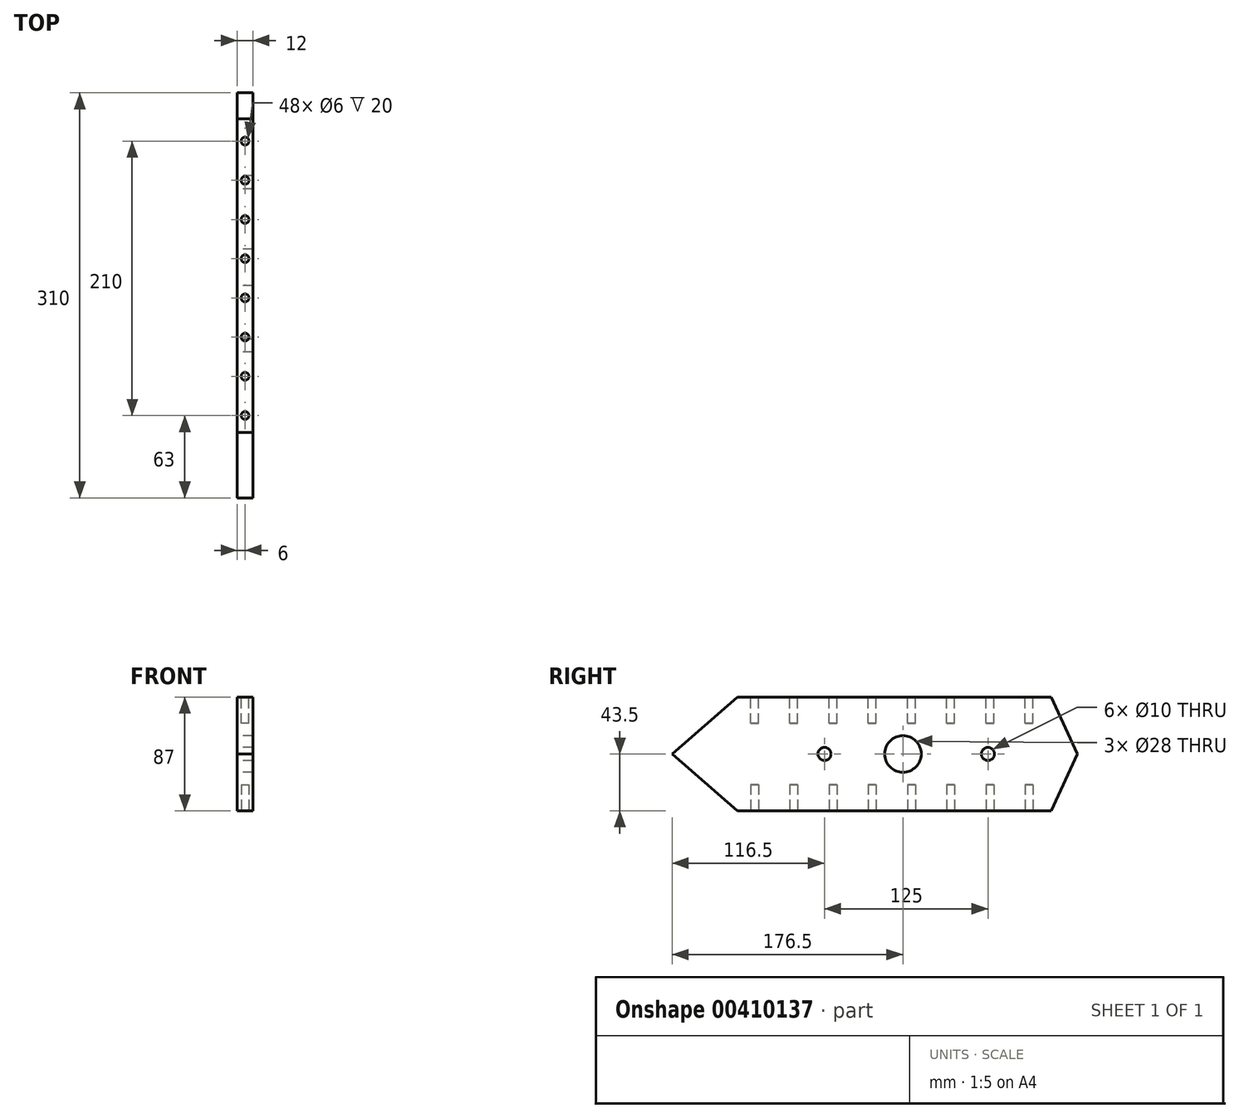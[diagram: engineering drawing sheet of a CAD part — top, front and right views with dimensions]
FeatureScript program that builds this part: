
annotation { "Feature Type Name" : "Feature", "Feature Type Description" : "" }
export const myFeature = defineFeature(function(context is Context, id is Id, definition is map)
    precondition{}
    {
        {
            var Q0;
            Q0=qCreatedBy(makeId("Right.planeOp"),FACE);
            var sketch = newSketch(context, id + "F0", { "sketchPlane" : qUnion([Q0])});
            skLineSegment(sketch, "E0.bottom", {"start": v(0, 0) * mm, "end": v(240, 0) * mm});
            skLineSegment(sketch, "E0.top", {"start": v(0, 87) * mm, "end": v(240, 87) * mm});
            skLineSegment(sketch, "E0.left", {"start": v(0, 0) * mm, "end": v(0, 87) * mm, "construction": true});
            skLineSegment(sketch, "E0.right", {"start": v(240, 0) * mm, "end": v(240, 87) * mm, "construction": true});
            skLineSegment(sketch, "E1", {"start": v(0, 43.5) * mm, "end": v(240, 43.5) * mm, "construction": true});
            skPoint(sketch, "E2", {"position": v(126.5, 43.5) * mm});
            skLineSegment(sketch, "E3", {"start": v(240, 87) * mm, "end": v(260, 43.5) * mm});
            skLineSegment(sketch, "E4", {"start": v(260, 43.5) * mm, "end": v(240, 0) * mm});
            skLineSegment(sketch, "E5", {"start": v(0, 87) * mm, "end": v(-50, 43.5) * mm});
            skLineSegment(sketch, "E6", {"start": v(-50, 43.5) * mm, "end": v(0, 0) * mm});
            skLineSegment(sketch, "E7", {"start": v(240, 43.5) * mm, "end": v(260, 43.5) * mm, "construction": true});
            skLineSegment(sketch, "E8", {"start": v(0, 43.5) * mm, "end": v(-50, 43.5) * mm, "construction": true});
            skCircle(sketch, "E9", {"center": v(126.5, 43.5) * mm, "radius": 14 * mm});
            skCircle(sketch, "E10", {"center": v(191.5, 43.5) * mm, "radius": 5 * mm});
            skCircle(sketch, "E11", {"center": v(66.5, 43.5) * mm, "radius": 5 * mm});
            skSolve(sketch);
        }
        {
            var Q0;
            Q0=qSketchRegion(id+"F0",true);
            extrude(context, id + "F1", {"entities" : qUnion([Q0]), "depth" : 12 * mm});
        }
        {
            var Q0;
            Q0=makeQuery(id+"F1.opExtrude","SWEPT_FACE",FACE,{"disambiguationData":[OSD([sQuery(id+"F0.wireOp",EDGE,"E0.top")])]});
            var sketch = newSketch(context, id + "F2", { "sketchPlane" : qUnion([Q0])});
            skLineSegment(sketch, "E12", {"start": v(6, 240) * mm, "end": v(6, 0) * mm, "construction": true});
            skCircle(sketch, "E13", {"center": v(6, 13) * mm, "radius": 3 * mm});
            skCircle(sketch, "E14.0.1.0", {"center": v(6, 43) * mm, "radius": 3 * mm});
            skCircle(sketch, "E14.0.2.0", {"center": v(6, 73) * mm, "radius": 3 * mm});
            skCircle(sketch, "E14.0.3.0", {"center": v(6, 103) * mm, "radius": 3 * mm});
            skCircle(sketch, "E14.0.4.0", {"center": v(6, 133) * mm, "radius": 3 * mm});
            skCircle(sketch, "E14.0.5.0", {"center": v(6, 163) * mm, "radius": 3 * mm});
            skCircle(sketch, "E14.0.6.0", {"center": v(6, 193) * mm, "radius": 3 * mm});
            skCircle(sketch, "E14.0.7.0", {"center": v(6, 223) * mm, "radius": 3 * mm});
            skLineSegment(sketch, "E14.direction1", {"start": v(6, 13) * mm, "end": v(31, 13) * mm, "construction": true});
            skLineSegment(sketch, "E14.direction2", {"start": v(6, 13) * mm, "end": v(6, 43) * mm, "construction": true});
            skSolve(sketch);
        }
        {
            var Q0;
            Q0 = qSketchRegion(id + "F2", true);
            extrude(context, id + "F3", {"entities" : qUnion([Q0]), "operationType" : NewBodyOperationType.REMOVE, "oppositeDirection" : true, "depth" : 20 * mm});
        }
        {
            var Q0;
            Q0=makeQuery(id+"F1.opExtrude","SWEPT_FACE",FACE,{"disambiguationData":[OSD([sQuery(id+"F0.wireOp",EDGE,"E0.bottom")])]});
            var sketch = newSketch(context, id + "F4", { "sketchPlane" : qUnion([Q0])});
            skLineSegment(sketch, "E15.0", {"start": v(6, -240) * mm, "end": v(6, 0) * mm});
            skCircle(sketch, "E15.1", {"center": v(6, -13) * mm, "radius": 3 * mm});
            skCircle(sketch, "E15.2", {"center": v(6, -43) * mm, "radius": 3 * mm});
            skCircle(sketch, "E15.3", {"center": v(6, -73) * mm, "radius": 3 * mm});
            skCircle(sketch, "E15.4", {"center": v(6, -103) * mm, "radius": 3 * mm});
            skCircle(sketch, "E15.5", {"center": v(6, -133) * mm, "radius": 3 * mm});
            skCircle(sketch, "E15.6", {"center": v(6, -163) * mm, "radius": 3 * mm});
            skCircle(sketch, "E15.7", {"center": v(6, -193) * mm, "radius": 3 * mm});
            skCircle(sketch, "E15.8", {"center": v(6, -223) * mm, "radius": 3 * mm});
            skLineSegment(sketch, "E15.9", {"start": v(6, -13) * mm, "end": v(31, -13) * mm});
            skLineSegment(sketch, "E15.10", {"start": v(6, -13) * mm, "end": v(6, -43) * mm});
            skSolve(sketch);
        }
        {
            var Q0;
            Q0 = qSketchRegion(id + "F4", true);
            extrude(context, id + "F5", {"entities" : qUnion([Q0]), "operationType" : NewBodyOperationType.REMOVE, "oppositeDirection" : true, "depth" : 20 * mm});
        }
    });
